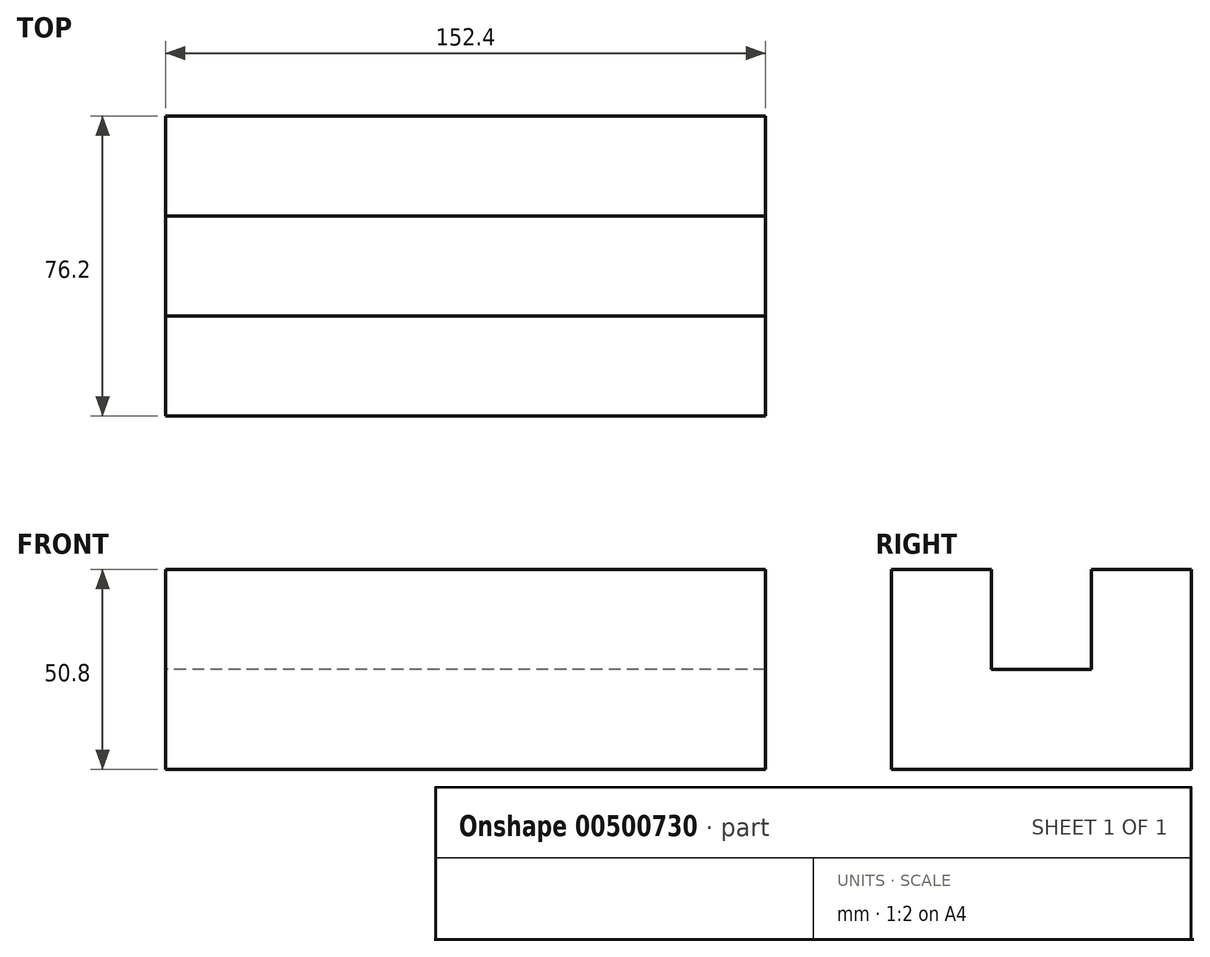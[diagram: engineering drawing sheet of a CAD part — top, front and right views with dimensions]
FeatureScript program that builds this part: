
annotation { "Feature Type Name" : "Feature", "Feature Type Description" : "" }
export const myFeature = defineFeature(function(context is Context, id is Id, definition is map)
    precondition{}
    {
        {
            var Q0;
            Q0=qCreatedBy(makeId("Right.planeOp"),FACE);
            var sketch = newSketch(context, id + "F0", { "sketchPlane" : qUnion([Q0])});
            skLineSegment(sketch, "E0", {"start": v(-71.7, 53.02) * mm, "end": v(-71.7, 2.22) * mm});
            skLineSegment(sketch, "E1", {"start": v(-71.7, 2.22) * mm, "end": v(4.5, 2.22) * mm});
            skLineSegment(sketch, "E2", {"start": v(4.5, 2.22) * mm, "end": v(4.5, 53.02) * mm});
            skLineSegment(sketch, "E3", {"start": v(4.5, 53.02) * mm, "end": v(-20.9, 53.02) * mm});
            skLineSegment(sketch, "E4", {"start": v(-20.9, 53.02) * mm, "end": v(-20.9, 27.62) * mm});
            skLineSegment(sketch, "E5", {"start": v(-20.9, 27.62) * mm, "end": v(-46.3, 27.62) * mm});
            skLineSegment(sketch, "E6", {"start": v(-46.3, 27.62) * mm, "end": v(-46.3, 53.02) * mm});
            skLineSegment(sketch, "E7", {"start": v(-46.3, 53.02) * mm, "end": v(-71.7, 53.02) * mm});
            skSolve(sketch);
        }
        {
            var Q0;
            Q0 = qSketchRegion(id + "F0", true);
            extrude(context, id + "F1", {"entities" : qUnion([Q0]), "depth" : 152.4 * mm});
        }
    });
